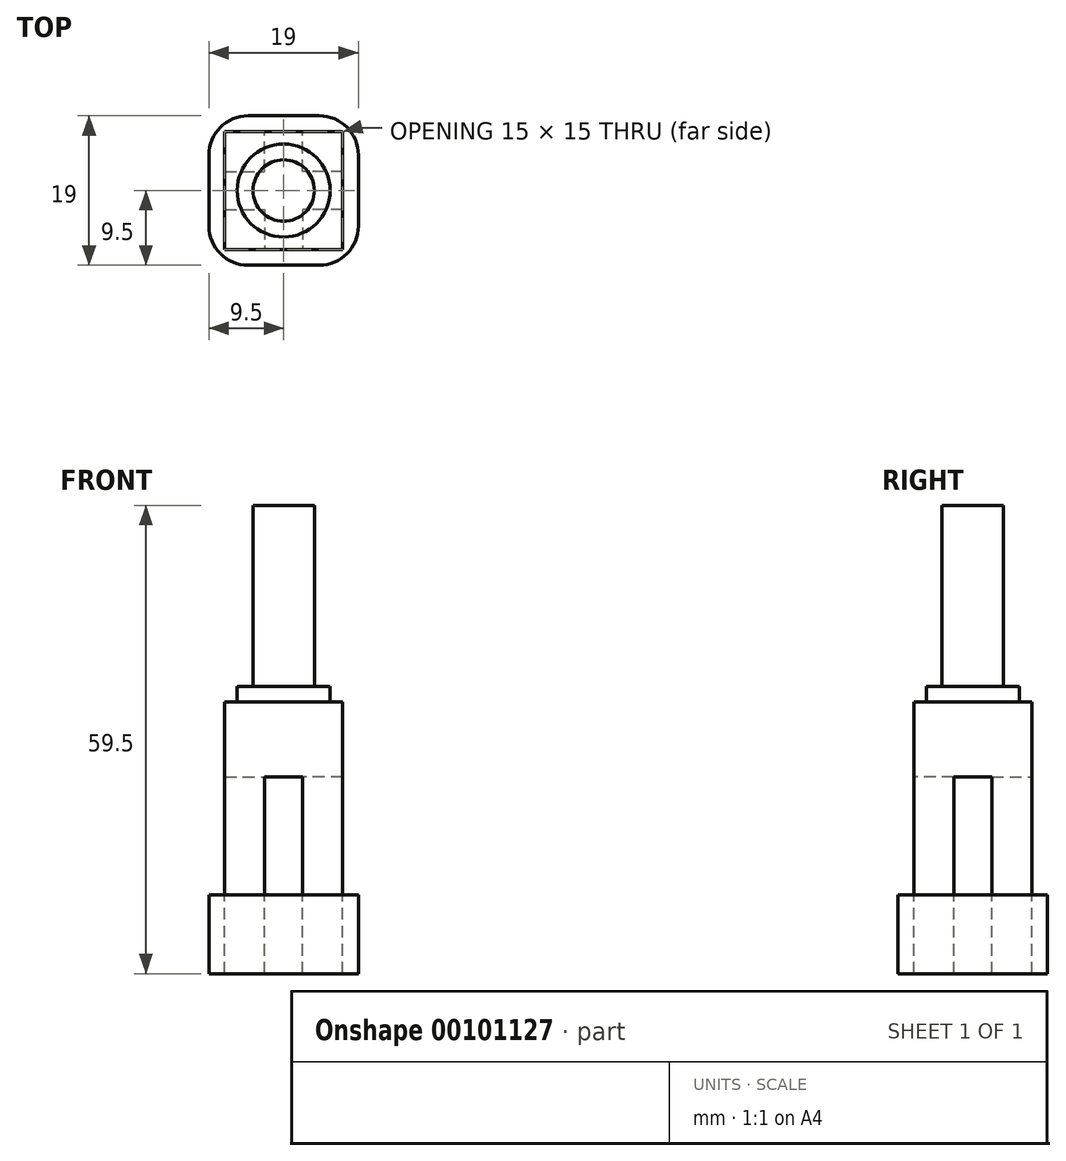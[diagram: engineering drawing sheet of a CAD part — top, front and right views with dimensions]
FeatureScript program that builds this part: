
annotation { "Feature Type Name" : "Feature", "Feature Type Description" : "" }
export const myFeature = defineFeature(function(context is Context, id is Id, definition is map)
    precondition{}
    {
        {
            var Q0;
            Q0=qCreatedBy(makeId("Top.planeOp"),FACE);
            var sketch = newSketch(context, id + "F0", { "sketchPlane" : qUnion([Q0])});
            skCircle(sketch, "E0", {"center": v(0, 0) * mm, "radius": 3.9 * mm});
            skLineSegment(sketch, "E1", {"start": v(-3.74, 1.1) * mm, "end": v(3.74, 1.1) * mm});
            skLineSegment(sketch, "E2", {"start": v(-3.74, -1.1) * mm, "end": v(3.74, -1.1) * mm});
            skLineSegment(sketch, "E3.bottom", {"start": v(-7.5, 7.5) * mm, "end": v(7.5, 7.5) * mm});
            skLineSegment(sketch, "E3.top", {"start": v(-7.5, -7.5) * mm, "end": v(7.5, -7.5) * mm});
            skLineSegment(sketch, "E3.left", {"start": v(-7.5, 7.5) * mm, "end": v(-7.5, -7.5) * mm});
            skLineSegment(sketch, "E3.right", {"start": v(7.5, 7.5) * mm, "end": v(7.5, -7.5) * mm});
            skSolve(sketch);
        }
        {
            var Q0;
            Q0=makeQuery(id+"F0.imprint","IMPRINT",FACE,{"disambiguationData":[TD([[makeQuery(id+"F0.imprint","IMPRINT",EDGE,{"derivedFrom":sQuery(id+"F0.wireOp",EDGE,"E3.bottom")}),-1.0]])]});
            var Q1;
            {var subQ0=sQuery(id+"F0.wireOp",EDGE,"E2");Q1=makeQuery(id+"F0.imprint","IMPRINT",FACE,{"disambiguationData":[TD([[makeQuery(id+"F0.imprint","IMPRINT",EDGE,{"derivedFrom":subQ0}),-1.0]])]});}
            var Q2;
            {var subQ0=sQuery(id+"F0.wireOp",EDGE,"E1");Q2=makeQuery(id+"F0.imprint","IMPRINT",FACE,{"disambiguationData":[TD([[makeQuery(id+"F0.imprint","IMPRINT",EDGE,{"derivedFrom":subQ0}),1.0]])]});}
            var Q3;
            {var subQ0=sQuery(id+"F0.wireOp",EDGE,"E1");Q3=makeQuery(id+"F0.imprint","IMPRINT",FACE,{"disambiguationData":[TD([[makeQuery(id+"F0.imprint","IMPRINT",EDGE,{"derivedFrom":subQ0}),-1.0]])]});}
            extrude(context, id + "F1", {"entities" : qUnion([Q0, Q1, Q2, Q3]), "depth" : 7.5 * mm});
        }
        {
            var Q0;
            {var subQ0=sQuery(id+"F0.wireOp",EDGE,"E1");Q0=makeQuery(id+"F0.imprint","IMPRINT",FACE,{"disambiguationData":[TD([[makeQuery(id+"F0.imprint","IMPRINT",EDGE,{"derivedFrom":subQ0}),-1.0]])]});}
            extrude(context, id + "F2", {"entities" : qUnion([Q0]), "operationType" : NewBodyOperationType.ADD, "depth" : 2 * mm});
        }
        {
            var Q0;
            {var subQ0=sQuery(id+"F0.wireOp",EDGE,"E2");var subQ1=sQuery(id+"F0.wireOp",EDGE,"E1");var subQ2=sQuery(id+"F0.wireOp",EDGE,"E0");Q0=makeQuery(id+"F2.boolean.opBoolean","MERGE",FACE,{"derivedFrom":[makeQuery(id+"F1.opExtrude","CAP_FACE",FACE,{"disambiguationData":[OSD([subQ2,subQ1,subQ0,sQuery(id+"F0.wireOp",EDGE,"E3.bottom"),sQuery(id+"F0.wireOp",EDGE,"E3.top"),sQuery(id+"F0.wireOp",EDGE,"E3.left"),sQuery(id+"F0.wireOp",EDGE,"E3.right")])],"isStart":true}),makeQuery(id+"F2.opExtrude","CAP_FACE",FACE,{"disambiguationData":[OSD([subQ2,subQ1,subQ0])],"isStart":true})]});}
            var sketch = newSketch(context, id + "F3", { "sketchPlane" : qUnion([Q0])});
            skPoint(sketch, "E4", {"position": v(-7.5, -2.4) * mm});
            skPoint(sketch, "E5", {"position": v(-2.4, -7.5) * mm});
            skLineSegment(sketch, "E6", {"start": v(-7.5, -2.4) * mm, "end": v(-2.4, -2.4) * mm});
            skLineSegment(sketch, "E7", {"start": v(-2.4, -2.4) * mm, "end": v(-2.4, -7.5) * mm});
            skLineSegment(sketch, "E8.MirrorCS", {"start": v(7.5, -2.4) * mm, "end": v(2.4, -2.4) * mm});
            skLineSegment(sketch, "E9.MirrorCS", {"start": v(2.4, -2.4) * mm, "end": v(2.4, -7.5) * mm});
            skLineSegment(sketch, "E10.MirrorCS", {"start": v(-7.5, 2.4) * mm, "end": v(-2.4, 2.4) * mm});
            skLineSegment(sketch, "E11.MirrorCS", {"start": v(-2.4, 2.4) * mm, "end": v(-2.4, 7.5) * mm});
            skLineSegment(sketch, "E12.MirrorCS", {"start": v(7.5, 2.4) * mm, "end": v(2.4, 2.4) * mm});
            skLineSegment(sketch, "E13.MirrorCS", {"start": v(2.4, 2.4) * mm, "end": v(2.4, 7.5) * mm});
            skSolve(sketch);
        }
        {
            var Q0;
            {var subQ0=sQuery(id+"F3.wireOp",EDGE,"E6");Q0=makeQuery(id+"F3.imprint","IMPRINT",FACE,{"disambiguationData":[TD([[makeQuery(id+"F3.imprint","IMPRINT",EDGE,{"derivedFrom":subQ0}),-1.0]])]});}
            var Q1;
            {var subQ0=sQuery(id+"F3.wireOp",EDGE,"E8.MirrorCS");Q1=makeQuery(id+"F3.imprint","IMPRINT",FACE,{"disambiguationData":[TD([[makeQuery(id+"F3.imprint","IMPRINT",EDGE,{"derivedFrom":subQ0}),1.0]])]});}
            var Q2;
            {var subQ0=sQuery(id+"F3.wireOp",EDGE,"E12.MirrorCS");Q2=makeQuery(id+"F3.imprint","IMPRINT",FACE,{"disambiguationData":[TD([[makeQuery(id+"F3.imprint","IMPRINT",EDGE,{"derivedFrom":subQ0}),-1.0]])]});}
            var Q3;
            {var subQ0=sQuery(id+"F3.wireOp",EDGE,"E10.MirrorCS");Q3=makeQuery(id+"F3.imprint","IMPRINT",FACE,{"disambiguationData":[TD([[makeQuery(id+"F3.imprint","IMPRINT",EDGE,{"derivedFrom":subQ0}),1.0]])]});}
            extrude(context, id + "F4", {"entities" : qUnion([Q0, Q1, Q2, Q3]), "operationType" : NewBodyOperationType.ADD, "depth" : 25 * mm});
        }
        {
            var Q0;
            Q0=makeQuery(id+"F1.opExtrude","CAP_FACE",FACE,{"disambiguationData":[OSD([sQuery(id+"F0.wireOp",EDGE,"E0"),sQuery(id+"F0.wireOp",EDGE,"E1"),sQuery(id+"F0.wireOp",EDGE,"E2"),sQuery(id+"F0.wireOp",EDGE,"E3.bottom"),sQuery(id+"F0.wireOp",EDGE,"E3.top"),sQuery(id+"F0.wireOp",EDGE,"E3.left"),sQuery(id+"F0.wireOp",EDGE,"E3.right")])],"isStart":false});
            extrude(context, id + "F5", {"entities" : qUnion([Q0]), "operationType" : NewBodyOperationType.ADD, "depth" : 2 * mm});
        }
        {
            var Q0;
            Q0=makeQuery(id+"F4.opExtrude","CAP_FACE",FACE,{"disambiguationData":[OSD([sQuery(id+"F0.wireOp",EDGE,"E3.top"),sQuery(id+"F0.wireOp",EDGE,"E3.left"),sQuery(id+"F3.wireOp",EDGE,"E10.MirrorCS"),sQuery(id+"F3.wireOp",EDGE,"E11.MirrorCS")])],"isStart":false});
            var sketch = newSketch(context, id + "F6", { "sketchPlane" : qUnion([Q0])});
            skLineSegment(sketch, "E14.bottom", {"start": v(-7.5, 7.5) * mm, "end": v(7.5, 7.5) * mm});
            skLineSegment(sketch, "E14.top", {"start": v(-7.5, -7.5) * mm, "end": v(7.5, -7.5) * mm});
            skLineSegment(sketch, "E14.left", {"start": v(-7.5, 7.5) * mm, "end": v(-7.5, -7.5) * mm});
            skLineSegment(sketch, "E14.right", {"start": v(7.5, 7.5) * mm, "end": v(7.5, -7.5) * mm});
            skLineSegment(sketch, "E15.bottom", {"start": v(-9.5, -9.5) * mm, "end": v(9.5, -9.5) * mm});
            skLineSegment(sketch, "E15.top", {"start": v(-9.5, 9.5) * mm, "end": v(9.5, 9.5) * mm});
            skLineSegment(sketch, "E15.left", {"start": v(-9.5, -9.5) * mm, "end": v(-9.5, 9.5) * mm});
            skLineSegment(sketch, "E15.right", {"start": v(9.5, -9.5) * mm, "end": v(9.5, 9.5) * mm});
            skPoint(sketch, "E15.middle", {"position": v(0, 0) * mm});
            skSolve(sketch);
        }
        {
            var Q0;
            {var subQ2=sQuery(id+"F6.wireOp",EDGE,"E14.top");Q0=makeQuery(id+"F6.imprint","IMPRINT",FACE,{"disambiguationData":[TD([[makeQuery(id+"F6.imprint","IMPRINT",EDGE,{"derivedFrom":subQ2}),-1.0]])]});}
            extrude(context, id + "F7", {"entities" : qUnion([Q0]), "operationType" : NewBodyOperationType.ADD, "oppositeDirection" : true, "depth" : 10 * mm});
        }
        {
            var Q0;
            Q0=makeQuery(id+"F7.opExtrude","SWEPT_EDGE",EDGE,{"disambiguationData":[OSD([sQuery(id+"F6.wireOp",EDGE,"E15.top"),sQuery(id+"F6.wireOp",EDGE,"E15.right")])]});
            var Q1;
            Q1=makeQuery(id+"F7.opExtrude","SWEPT_EDGE",EDGE,{"disambiguationData":[OSD([sQuery(id+"F6.wireOp",EDGE,"E15.bottom"),sQuery(id+"F6.wireOp",EDGE,"E15.right")])]});
            var Q2;
            Q2=makeQuery(id+"F7.opExtrude","SWEPT_EDGE",EDGE,{"disambiguationData":[OSD([sQuery(id+"F6.wireOp",EDGE,"E15.bottom"),sQuery(id+"F6.wireOp",EDGE,"E15.left")])]});
            var Q3;
            Q3=makeQuery(id+"F7.opExtrude","SWEPT_EDGE",EDGE,{"disambiguationData":[OSD([sQuery(id+"F6.wireOp",EDGE,"E15.top"),sQuery(id+"F6.wireOp",EDGE,"E15.left")])]});
            fillet(context, id + "F8", {"entities" : qUnion([Q0, Q1, Q2, Q3]), "radius" : 5 * mm, "tangentPropagation" : true, "allowEdgeOverflow" : false});
        }
        {
            var Q0;
            Q0=makeQuery(id+"F5.opExtrude","CAP_FACE",FACE,{"disambiguationData":[OSD([sQuery(id+"F0.wireOp",EDGE,"E3.bottom"),sQuery(id+"F0.wireOp",EDGE,"E3.top"),sQuery(id+"F0.wireOp",EDGE,"E3.left"),sQuery(id+"F0.wireOp",EDGE,"E3.right")])],"isStart":false});
            var sketch = newSketch(context, id + "F9", { "sketchPlane" : qUnion([Q0])});
            skCircle(sketch, "E16", {"center": v(0, 0) * mm, "radius": 3.9 * mm});
            skCircle(sketch, "E17", {"center": v(0, 0) * mm, "radius": 5.9 * mm});
            skSolve(sketch);
        }
        {
            var Q0;
            Q0=makeQuery(id+"F9.imprint","IMPRINT",FACE,{"disambiguationData":[TD([[makeQuery(id+"F9.imprint","IMPRINT",EDGE,{"derivedFrom":sQuery(id+"F9.wireOp",EDGE,"E16")}),-1.0]])]});
            extrude(context, id + "F10", {"entities" : qUnion([Q0]), "operationType" : NewBodyOperationType.ADD, "depth" : 2 * mm});
        }
        {
            var Q0;
            Q0=makeQuery(id+"F10.boolean.opBoolean","SPLIT",FACE,{"disambiguationData":[TD([makeQuery(id+"F10.opExtrude","SWEPT_FACE",FACE,{"disambiguationData":[OSD([sQuery(id+"F9.wireOp",EDGE,"E16")])]})])],"derivedFrom":makeQuery(id+"F5.opExtrude","CAP_FACE",FACE,{"disambiguationData":[OSD([sQuery(id+"F0.wireOp",EDGE,"E3.bottom"),sQuery(id+"F0.wireOp",EDGE,"E3.top"),sQuery(id+"F0.wireOp",EDGE,"E3.left"),sQuery(id+"F0.wireOp",EDGE,"E3.right")])],"isStart":false})});
            extrude(context, id + "F11", {"entities" : qUnion([Q0]), "operationType" : NewBodyOperationType.ADD, "depth" : 25 * mm});
        }
    });
